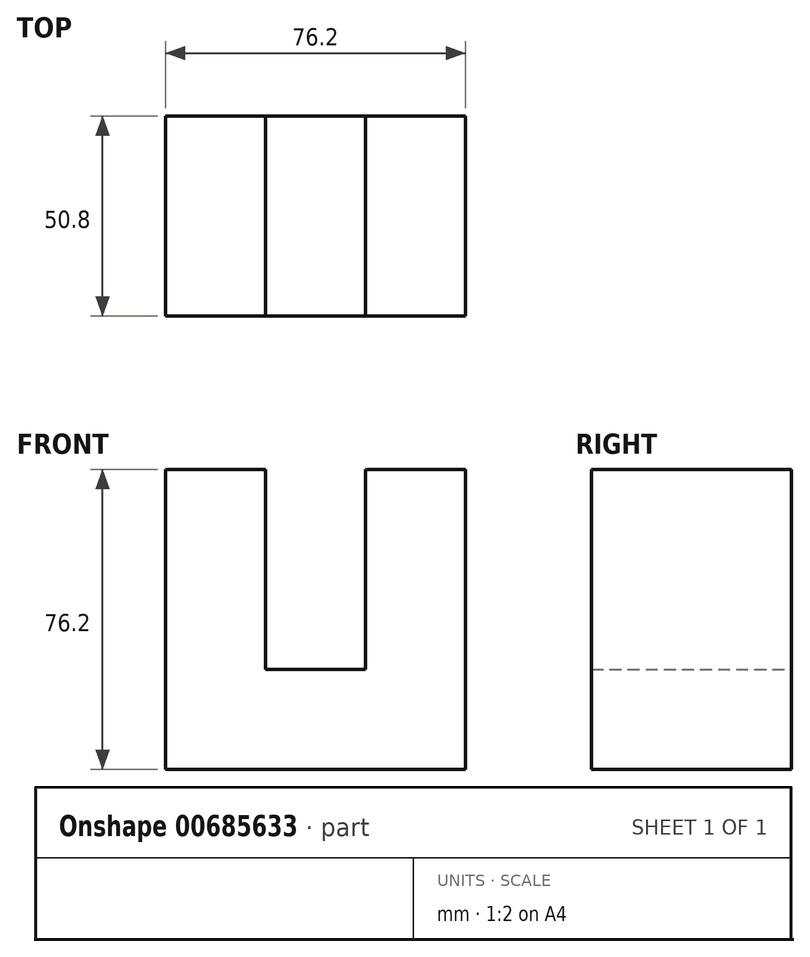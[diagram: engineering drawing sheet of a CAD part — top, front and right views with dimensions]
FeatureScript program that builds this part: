
annotation { "Feature Type Name" : "Feature", "Feature Type Description" : "" }
export const myFeature = defineFeature(function(context is Context, id is Id, definition is map)
    precondition{}
    {
        {
            var Q0;
            Q0=qCreatedBy(makeId("Front.planeOp"),FACE);
            var sketch = newSketch(context, id + "F0", { "sketchPlane" : qUnion([Q0])});
            skLineSegment(sketch, "E0", {"start": v(-50.8, 80.33) * mm, "end": v(-50.8, 4.13) * mm});
            skLineSegment(sketch, "E1", {"start": v(-50.8, 4.13) * mm, "end": v(25.4, 4.13) * mm});
            skLineSegment(sketch, "E2", {"start": v(25.4, 4.13) * mm, "end": v(25.4, 80.33) * mm});
            skLineSegment(sketch, "E3", {"start": v(25.4, 80.33) * mm, "end": v(0, 80.33) * mm});
            skLineSegment(sketch, "E4", {"start": v(0, 80.33) * mm, "end": v(0, 29.53) * mm});
            skLineSegment(sketch, "E5", {"start": v(0, 29.53) * mm, "end": v(-25.4, 29.53) * mm});
            skLineSegment(sketch, "E6", {"start": v(-25.4, 29.53) * mm, "end": v(-25.4, 80.33) * mm});
            skLineSegment(sketch, "E7", {"start": v(-25.4, 80.33) * mm, "end": v(-50.8, 80.33) * mm});
            skSolve(sketch);
        }
        {
            var Q0;
            Q0 = qSketchRegion(id + "F0", true);
            extrude(context, id + "F1", {"entities" : qUnion([Q0]), "depth" : 50.8 * mm, "offsetDistance" : 25.4 * mm});
        }
    });
